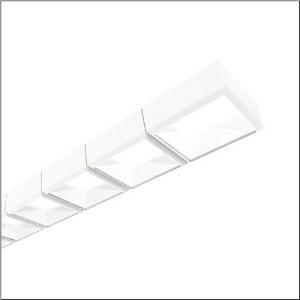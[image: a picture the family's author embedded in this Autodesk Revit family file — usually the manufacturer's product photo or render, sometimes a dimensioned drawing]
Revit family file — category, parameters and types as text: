
# Revit family: scriptus_11_5mz312d04wa
name_source: partatom
category: Lighting Fixtures
units: mm (PartAtom-declared; Revit-internal decimal feet)

## family parameters
Cut with Voids When Loaded = No
Host = Face
Light Source = No
Part Type = Normal
Room Calculation Point = No
Round Connector Dimension = Use Diameter
Shared = No

## types (1)
- Scriptus 11 (1 x LED 4000K / CRI = 80 (unbekannt), 1610 lm / 2410 lm, 4000K)
    Apparent Load = 62 VA
    CIE Flux Codes = - - - 0 100 / 82 95 99 100 100
    Color Rendering = 80
    Color Temperature = 4000K
    Default Elevation = 1800 mm
    Description = Scriptus 11, office luminaire, primary optical cover: lenses, CAT 2 (L<= 3000cd/m²), light emission: direct/indirect distribution, primary light characteristic: symmetric, installation type: suspended mounting, LED, rated luminous flux: 8.020lm, luminous efficacy: 130lm/W, light colour: 840, colour temperature: 4000K, control gear: DALI, with terminal, 5-pole, mains connection: 230V, AC, 50Hz, rated input power: 62W, LED, control gear: ECG DALI, housing, luminaire housing, of aluminium, traffic white (RAL 9016), length: 1.658mm, width: 114mm, height: 57mm, protection rating (complete): IP20, insulation class (complete): insulation class I (protective earthing), certification: CE, ENEC, VDE, protection symbol: F, permissible operating ambient temperature: 0..+35°C, standard: EN 50419, packaging unit: 1 piece
    Height = 57 mm
    Lamp = 1 x LED 4000K / CRI >= 80 (unbekannt)
    Lamp Light Flux = 1610 lm / 2410 lm
    Lamp count = 1
    Length = 1658 mm
    Luminous efficacy = 131 lm/W
    Manufacturer = Siteco
    ModVariant = No
    Model = 5MZ312D04WA
    Mounting Place = Ceiling
    Mounting Type = Pendant
    Number of Poles = 1
    OnlyDefault = Yes
    Power Factor = 1
    Product Name = Scriptus 11
    Product group = office luminaire | ceiling pendant
    ProductGroupID = 903
    Protection Class = Protection class I
    Protection Degree = IP 20
    RLX_Detail_Level = 1
    RLX_Emergency_Light_Flux = 0 lm
    RLX_Emergency_Type = 0
    RLX_Emergency_Type_DB = No
    RlxData = <blob elided: 31117 chars, md5=04664de8>
    Socket = socket
    Standby Power = 0 W
    System Light Flux = 8040 lm
    System Power = 62 W
    Type Comments = Product without accessories
    Type Image = l_1004839.jpg
    URL = http://relux.com
    VarID = ---
    Voltage = 0 V
    Weight = 0.00 kg
    Width = 114 mm

## geometry (parser evidence)
native form markers: Blend x4, Sweep x19
no freeform markers — native parametric forms only
